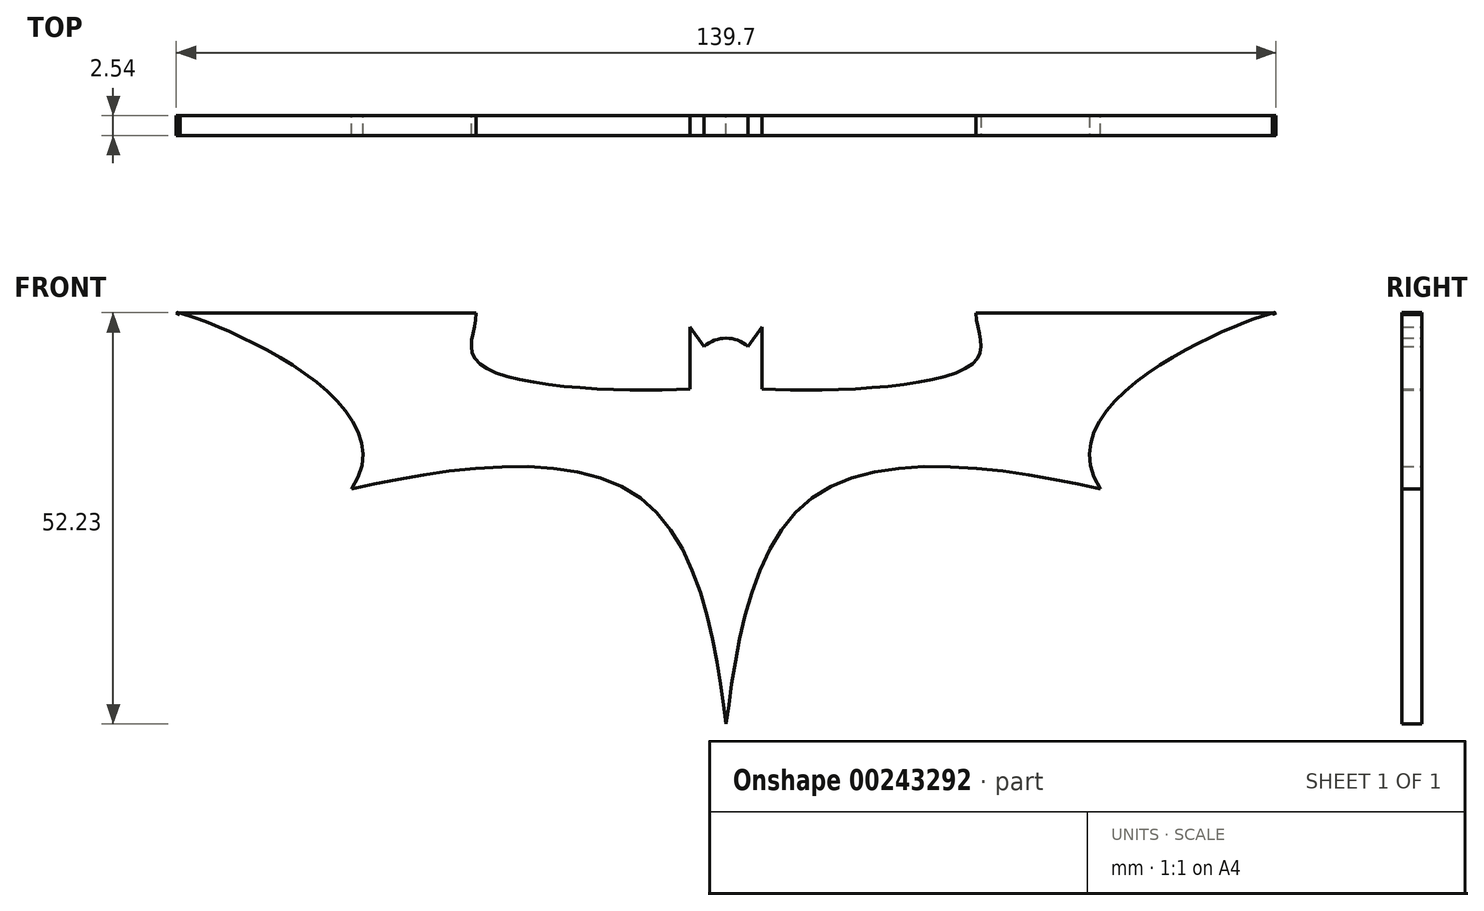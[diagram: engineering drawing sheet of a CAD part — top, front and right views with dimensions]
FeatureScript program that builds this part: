
annotation { "Feature Type Name" : "Feature", "Feature Type Description" : "" }
export const myFeature = defineFeature(function(context is Context, id is Id, definition is map)
    precondition{}
    {
        {
            var Q0;
            Q0=qCreatedBy(makeId("Front.planeOp"),FACE);
            var sketch = newSketch(context, id + "F0", { "sketchPlane" : qUnion([Q0])});
            skLineSegment(sketch, "E0", {"start": v(-4.56, 0) * mm, "end": v(-4.56, 7.91) * mm});
            skPoint(sketch, "E1.endSnap0", {"position": v(-4.56, 3.96) * mm});
            skFitSpline(sketch, "E2", {"points": [v(-4.56, 0) * mm, v(-31.72, 3.63) * mm, v(-31.75, 9.65) * mm], "startDerivative": vector(-37.95, -1.9) * mm, "endDerivative": vector(0.3, 19.05) * mm});
            skLineSegment(sketch, "E3", {"start": v(-31.75, 9.65) * mm, "end": v(-69.85, 9.65) * mm});
            skFitSpline(sketch, "E4", {"points": [v(-69.85, 9.65) * mm, v(-69.68, 9.62) * mm, v(-47.55, -12.66) * mm], "startDerivative": vector(25.35, -11.52) * mm, "endDerivative": vector(-27.04, -40.78) * mm});
            skFitSpline(sketch, "E5", {"points": [v(-47.55, -12.66) * mm, v(-10.86, -13.87) * mm, v(0, -42.53) * mm], "startDerivative": vector(62.92, 13.8) * mm, "endDerivative": vector(7.33, -52.9) * mm});
            skFitSpline(sketch, "E6.MirrorCS", {"points": [v(4.56, 0) * mm, v(31.72, 3.63) * mm, v(31.75, 9.65) * mm], "startDerivative": vector(37.95, -1.9) * mm, "endDerivative": vector(-0.3, 19.05) * mm});
            skLineSegment(sketch, "E7.MirrorCS", {"start": v(31.75, 9.65) * mm, "end": v(69.85, 9.65) * mm});
            skFitSpline(sketch, "E8.MirrorCS", {"points": [v(69.85, 9.65) * mm, v(69.68, 9.62) * mm, v(47.55, -12.66) * mm], "startDerivative": vector(-25.35, -11.52) * mm, "endDerivative": vector(27.04, -40.78) * mm});
            skFitSpline(sketch, "E9.MirrorCS", {"points": [v(47.55, -12.66) * mm, v(10.86, -13.87) * mm, v(0, -42.53) * mm], "startDerivative": vector(-62.92, 13.8) * mm, "endDerivative": vector(-7.33, -52.9) * mm});
            skLineSegment(sketch, "E10.MirrorCS", {"start": v(4.56, 0) * mm, "end": v(4.56, 7.91) * mm});
            skArc(sketch, "E11", {"start": v(2.8, 5.43) * mm, "mid": v(0, 6.46) * mm, "end": v(-2.8, 5.43) * mm});
            skLineSegment(sketch, "E12", {"start": v(-4.56, 7.91) * mm, "end": v(-2.8, 5.43) * mm});
            skLineSegment(sketch, "E13.MirrorCS", {"start": v(4.56, 7.91) * mm, "end": v(2.8, 5.43) * mm});
            skArc(sketch, "E14.MirrorC", {"start": v(-2.8, 5.43) * mm, "mid": v(-1.5, 6.2) * mm, "end": v(0, 6.46) * mm});
            skPoint(sketch, "E15.start.orphan", {"position": v(0, 8) * mm});
            skSolve(sketch);
        }
        {
            var Q0;
            Q0 = qSketchRegion(id + "F0", true);
            extrude(context, id + "F1", {"entities" : qUnion([Q0]), "depth" : 2.54 * mm});
        }
    });
